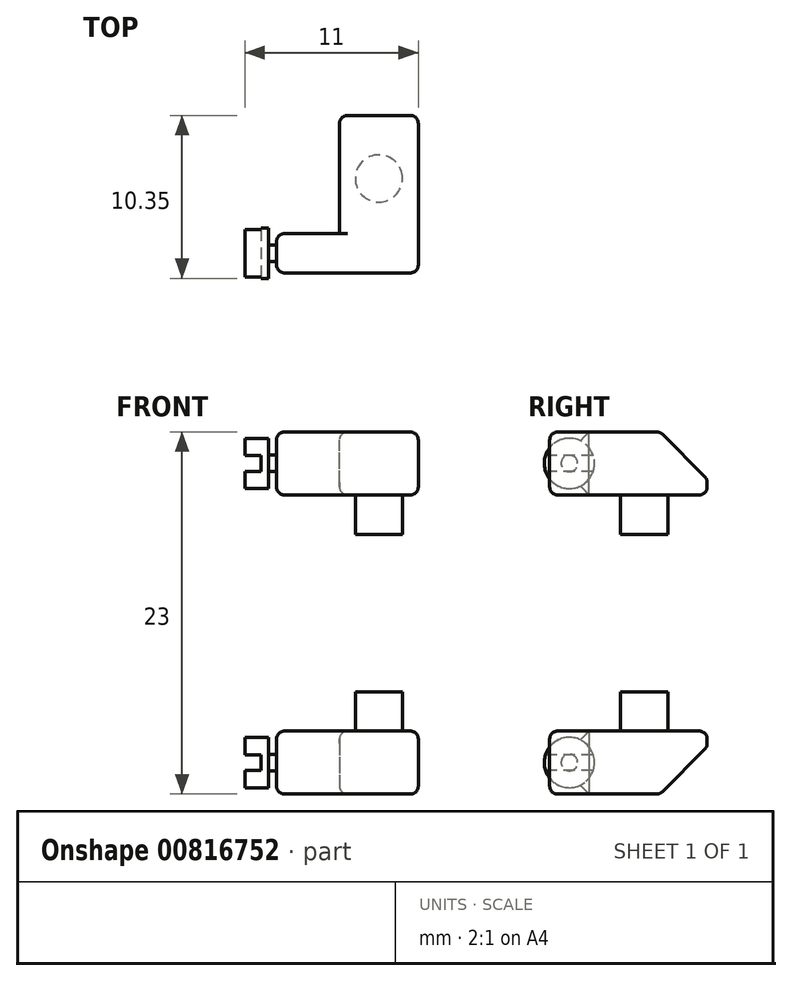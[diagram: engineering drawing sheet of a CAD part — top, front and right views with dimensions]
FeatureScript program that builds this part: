
annotation { "Feature Type Name" : "Feature", "Feature Type Description" : "" }
export const myFeature = defineFeature(function(context is Context, id is Id, definition is map)
    precondition{}
    {
        {
            var Q0;
            Q0=qCreatedBy(makeId("Top.planeOp"),FACE);
            var sketch = newSketch(context, id + "F0", { "sketchPlane" : qUnion([Q0])});
            skLineSegment(sketch, "E0.bottom", {"start": v(-2.5, 5) * mm, "end": v(2.5, 5) * mm});
            skLineSegment(sketch, "E0.top", {"start": v(-2.5, -5) * mm, "end": v(2.5, -5) * mm});
            skLineSegment(sketch, "E0.left", {"start": v(-2.5, 5) * mm, "end": v(-2.5, -5) * mm});
            skLineSegment(sketch, "E0.right", {"start": v(2.5, 5) * mm, "end": v(2.5, -5) * mm});
            skPoint(sketch, "E0.middle", {"position": v(0, 0) * mm});
            skSolve(sketch);
        }
        {
            var Q0;
            Q0 = qSketchRegion(id + "F0", true);
            extrude(context, id + "F1", {"entities" : qUnion([Q0]), "depth" : 4 * mm, "offsetDistance" : 25 * mm});
        }
        {
            var Q0;
            Q0=makeQuery(id+"F1.opExtrude","CAP_EDGE",EDGE,{"disambiguationData":[OSD([sQuery(id+"F0.wireOp",EDGE,"E0.bottom")])],"isStart":false});
            chamfer(context, id + "F2", {"entities" : qUnion([Q0]), "width" : 3 * mm, "tangentPropagation" : true});
        }
        {
            var Q0;
            Q0=makeQuery(id+"F1.opExtrude","CAP_FACE",FACE,{"disambiguationData":[OSD([sQuery(id+"F0.wireOp",EDGE,"E0.bottom"),sQuery(id+"F0.wireOp",EDGE,"E0.top"),sQuery(id+"F0.wireOp",EDGE,"E0.left"),sQuery(id+"F0.wireOp",EDGE,"E0.right")])],"isStart":true});
            var sketch = newSketch(context, id + "F3", { "sketchPlane" : qUnion([Q0])});
            skCircle(sketch, "E1", {"center": v(0, -1) * mm, "radius": 1.5 * mm});
            skPoint(sketch, "E2.start.orphan", {"position": v(0, 0) * mm});
            skSolve(sketch);
        }
        {
            var Q0;
            Q0 = qSketchRegion(id + "F3", true);
            extrude(context, id + "F4", {"entities" : qUnion([Q0]), "operationType" : NewBodyOperationType.ADD, "depth" : 2.5 * mm, "offsetDistance" : 25 * mm});
        }
        {
            var Q0;
            Q0=makeQuery(id+"F1.opExtrude","SWEPT_FACE",FACE,{"disambiguationData":[OSD([sQuery(id+"F0.wireOp",EDGE,"E0.left")])]});
            var sketch = newSketch(context, id + "F5", { "sketchPlane" : qUnion([Q0])});
            skLineSegment(sketch, "E3.bottom", {"start": v(5, 0) * mm, "end": v(2.5, 0) * mm});
            skLineSegment(sketch, "E3.top", {"start": v(5, 4) * mm, "end": v(2.5, 4) * mm});
            skLineSegment(sketch, "E3.left", {"start": v(5, 0) * mm, "end": v(5, 4) * mm});
            skLineSegment(sketch, "E3.right", {"start": v(2.5, 0) * mm, "end": v(2.5, 4) * mm});
            skSolve(sketch);
        }
        {
            var Q0;
            {var subQ0=sQuery(id+"F5.wireOp",EDGE,"E3.bottom");Q0=makeQuery(id+"F5.imprint","IMPRINT",FACE,{"disambiguationData":[TD([[makeQuery(id+"F5.imprint","IMPRINT",EDGE,{"derivedFrom":subQ0}),-1.0]])]});}
            var Q1;
            {var subQ0=sQuery(id+"F5.wireOp",EDGE,"E3.left");var subQ1=sQuery(id+"F0.wireOp",EDGE,"E0.left");var subQ2=makeQuery(id+"F1.opExtrude","SWEPT_FACE",FACE,{"disambiguationData":[OSD([subQ1])]});var subQ3=makeQuery(id+"FWwU1mPq5ux4r18_1.opFillet","BLEND_EDGE",EDGE,{"blendedFrom":[makeQuery(id+"F1.opExtrude","CAP_EDGE",EDGE,{"disambiguationData":[OSD([subQ1])],"isStart":true}),subQ2],"blendedInto":[subQ2]});var subQ4=makeQuery(id+"F5.imprint","INTERSECT",VERTEX,{"derivedFrom":[subQ3,subQ0]});var subQ5=makeQuery(id+"FWwU1mPq5ux4r18_1.opFillet","BLEND_EDGE",EDGE,{"blendedFrom":[makeQuery(id+"F1.opExtrude","CAP_EDGE",EDGE,{"disambiguationData":[OSD([subQ1])],"isStart":false}),subQ2],"blendedInto":[subQ2]});var subQ6=makeQuery(id+"F5.imprint","INTERSECT",VERTEX,{"derivedFrom":[subQ5,subQ0]});Q1=makeQuery(id+"F5.imprint","IMPRINT",FACE,{"disambiguationData":[TD([[makeQuery(id+"F5.imprint","IMPRINT",EDGE,{"disambiguationData":[TD([[subQ4,1.0],[subQ6,-1.0]])],"derivedFrom":subQ0}),-1.0]])]});}
            var Q2;
            {var subQ0=sQuery(id+"F5.wireOp",EDGE,"E3.top");Q2=makeQuery(id+"F5.imprint","IMPRINT",FACE,{"disambiguationData":[TD([[makeQuery(id+"F5.imprint","IMPRINT",EDGE,{"derivedFrom":subQ0}),1.0]])]});}
            extrude(context, id + "F6", {"entities" : qUnion([Q0, Q1, Q2]), "operationType" : NewBodyOperationType.ADD, "depth" : 4 * mm, "offsetDistance" : 25 * mm});
        }
        {
            var Q0;
            Q0=makeQuery(id+"F6.opExtrude","CAP_EDGE",EDGE,{"disambiguationData":[OSD([sQuery(id+"F5.wireOp",EDGE,"E3.right")])],"isStart":true});
            var Q1;
            Q1=makeQuery(id+"F1.opExtrude","SWEPT_EDGE",EDGE,{"disambiguationData":[OSD([sQuery(id+"F0.wireOp",EDGE,"E0.top"),sQuery(id+"F0.wireOp",EDGE,"E0.right")])]});
            var Q2;
            Q2=makeQuery(id+"F1.opExtrude","CAP_EDGE",EDGE,{"disambiguationData":[OSD([sQuery(id+"F0.wireOp",EDGE,"E0.bottom")])],"isStart":true});
            var Q3;
            {var subQ0=sQuery(id+"F0.wireOp",EDGE,"E0.bottom");Q3=makeQuery(id+"F2.opChamfer","BLEND_EDGE",EDGE,{"blendedFrom":[makeQuery(id+"F1.opExtrude","CAP_EDGE",EDGE,{"disambiguationData":[OSD([subQ0])],"isStart":false}),makeQuery(id+"F1.opExtrude","SWEPT_FACE",FACE,{"disambiguationData":[OSD([subQ0])]})],"blendedInto":[makeQuery(id+"F1.opExtrude","SWEPT_FACE",FACE,{"disambiguationData":[OSD([subQ0])]})]});}
            var Q4;
            Q4=makeQuery(id+"F2.opChamfer","BLEND_EDGE",EDGE,{"blendedFrom":[makeQuery(id+"F1.opExtrude","CAP_EDGE",EDGE,{"disambiguationData":[OSD([sQuery(id+"F0.wireOp",EDGE,"E0.bottom")])],"isStart":false}),makeQuery(id+"F1.opExtrude","SWEPT_FACE",FACE,{"disambiguationData":[OSD([sQuery(id+"F0.wireOp",EDGE,"E0.right")])]})],"blendedInto":[makeQuery(id+"F1.opExtrude","SWEPT_FACE",FACE,{"disambiguationData":[OSD([sQuery(id+"F0.wireOp",EDGE,"E0.right")])]})]});
            var Q5;
            {var subQ0=sQuery(id+"F0.wireOp",EDGE,"E0.bottom");Q5=makeQuery(id+"F2.opChamfer","BLEND_EDGE",EDGE,{"blendedFrom":[makeQuery(id+"F1.opExtrude","CAP_EDGE",EDGE,{"disambiguationData":[OSD([subQ0])],"isStart":false}),makeQuery(id+"F1.opExtrude","CAP_FACE",FACE,{"disambiguationData":[OSD([subQ0,sQuery(id+"F0.wireOp",EDGE,"E0.top"),sQuery(id+"F0.wireOp",EDGE,"E0.left"),sQuery(id+"F0.wireOp",EDGE,"E0.right")])],"isStart":false})],"blendedInto":[makeQuery(id+"F1.opExtrude","CAP_FACE",FACE,{"disambiguationData":[OSD([subQ0,sQuery(id+"F0.wireOp",EDGE,"E0.top"),sQuery(id+"F0.wireOp",EDGE,"E0.left"),sQuery(id+"F0.wireOp",EDGE,"E0.right")])],"isStart":false})]});}
            var Q6;
            Q6=makeQuery(id+"F1.opExtrude","SWEPT_EDGE",EDGE,{"disambiguationData":[OSD([sQuery(id+"F0.wireOp",EDGE,"E0.bottom"),sQuery(id+"F0.wireOp",EDGE,"E0.right")])]});
            var Q7;
            Q7=makeQuery(id+"F2.opChamfer","BLEND_EDGE",EDGE,{"blendedFrom":[makeQuery(id+"F1.opExtrude","CAP_EDGE",EDGE,{"disambiguationData":[OSD([sQuery(id+"F0.wireOp",EDGE,"E0.bottom")])],"isStart":false}),makeQuery(id+"F1.opExtrude","SWEPT_FACE",FACE,{"disambiguationData":[OSD([sQuery(id+"F0.wireOp",EDGE,"E0.left")])]})],"blendedInto":[makeQuery(id+"F1.opExtrude","SWEPT_FACE",FACE,{"disambiguationData":[OSD([sQuery(id+"F0.wireOp",EDGE,"E0.left")])]})]});
            var Q8;
            Q8=makeQuery(id+"F1.opExtrude","SWEPT_EDGE",EDGE,{"disambiguationData":[OSD([sQuery(id+"F0.wireOp",EDGE,"E0.bottom"),sQuery(id+"F0.wireOp",EDGE,"E0.left")])]});
            var Q9;
            Q9=makeQuery(id+"F1.opExtrude","CAP_EDGE",EDGE,{"disambiguationData":[OSD([sQuery(id+"F0.wireOp",EDGE,"E0.left")])],"isStart":true});
            var Q10;
            Q10=makeQuery(id+"F1.opExtrude","CAP_EDGE",EDGE,{"disambiguationData":[OSD([sQuery(id+"F0.wireOp",EDGE,"E0.right")])],"isStart":true});
            var Q11;
            Q11=makeQuery(id+"F6.boolean.opBoolean","MERGE",EDGE,{"derivedFrom":[makeQuery(id+"F1.opExtrude","CAP_EDGE",EDGE,{"disambiguationData":[OSD([sQuery(id+"F0.wireOp",EDGE,"E0.top")])],"isStart":true}),makeQuery(id+"F6.opExtrude","SWEPT_EDGE",EDGE,{"disambiguationData":[OSD([sQuery(id+"F5.wireOp",EDGE,"E3.bottom"),sQuery(id+"F5.wireOp",EDGE,"E3.left")])]})]});
            var Q12;
            Q12=makeQuery(id+"F6.boolean.opBoolean","MERGE",EDGE,{"derivedFrom":[makeQuery(id+"F1.opExtrude","CAP_EDGE",EDGE,{"disambiguationData":[OSD([sQuery(id+"F0.wireOp",EDGE,"E0.top")])],"isStart":false}),makeQuery(id+"F6.opExtrude","SWEPT_EDGE",EDGE,{"disambiguationData":[OSD([sQuery(id+"F5.wireOp",EDGE,"E3.top"),sQuery(id+"F5.wireOp",EDGE,"E3.left")])]})]});
            var Q13;
            Q13=makeQuery(id+"F1.opExtrude","CAP_EDGE",EDGE,{"disambiguationData":[OSD([sQuery(id+"F0.wireOp",EDGE,"E0.right")])],"isStart":false});
            var Q14;
            Q14=makeQuery(id+"F1.opExtrude","CAP_EDGE",EDGE,{"disambiguationData":[OSD([sQuery(id+"F0.wireOp",EDGE,"E0.left")])],"isStart":false});
            var Q15;
            Q15=makeQuery(id+"F6.opExtrude","CAP_EDGE",EDGE,{"disambiguationData":[OSD([sQuery(id+"F5.wireOp",EDGE,"E3.left")])],"isStart":false});
            var Q16;
            Q16=makeQuery(id+"F6.opExtrude","CAP_EDGE",EDGE,{"disambiguationData":[OSD([sQuery(id+"F5.wireOp",EDGE,"E3.top")])],"isStart":false});
            var Q17;
            Q17=makeQuery(id+"F6.opExtrude","CAP_EDGE",EDGE,{"disambiguationData":[OSD([sQuery(id+"F5.wireOp",EDGE,"E3.right")])],"isStart":false});
            var Q18;
            Q18=makeQuery(id+"F6.opExtrude","CAP_EDGE",EDGE,{"disambiguationData":[OSD([sQuery(id+"F5.wireOp",EDGE,"E3.bottom")])],"isStart":false});
            fillet(context, id + "F7", {"entities" : qUnion([Q0, Q1, Q2, Q3, Q4, Q5, Q6, Q7, Q8, Q9, Q10, Q11, Q12, Q13, Q14, Q15, Q16, Q17, Q18]), "radius" : 0.5 * mm, "tangentPropagation" : true, "allowEdgeOverflow" : false});
        }
        {
            var Q0;
            Q0=makeQuery(id+"F6.opExtrude","CAP_FACE",FACE,{"disambiguationData":[OSD([sQuery(id+"F5.wireOp",EDGE,"E3.bottom"),sQuery(id+"F5.wireOp",EDGE,"E3.top"),sQuery(id+"F5.wireOp",EDGE,"E3.left"),sQuery(id+"F5.wireOp",EDGE,"E3.right")])],"isStart":false});
            var sketch = newSketch(context, id + "F8", { "sketchPlane" : qUnion([Q0])});
            skCircle(sketch, "E4", {"center": v(3.75, 2) * mm, "radius": 0.53 * mm});
            skPoint(sketch, "E4.centerSnap0", {"position": v(3, 2) * mm});
            skPoint(sketch, "E4.centerSnap1", {"position": v(3.75, 0.5) * mm});
            skSolve(sketch);
        }
        {
            var Q0;
            Q0 = qSketchRegion(id + "F8", true);
            extrude(context, id + "F9", {"entities" : qUnion([Q0]), "operationType" : NewBodyOperationType.ADD, "depth" : 0.5 * mm, "offsetDistance" : 25 * mm});
        }
        {
            var Q0;
            Q0=makeQuery(id+"F9.opExtrude","CAP_FACE",FACE,{"disambiguationData":[OSD([sQuery(id+"F8.wireOp",EDGE,"E4")])],"isStart":false});
            var sketch = newSketch(context, id + "F10", { "sketchPlane" : qUnion([Q0])});
            skCircle(sketch, "E5", {"center": v(3.75, 2) * mm, "radius": 1.6 * mm});
            skSolve(sketch);
        }
        {
            var Q0;
            Q0 = qSketchRegion(id + "F10", true);
            extrude(context, id + "F11", {"entities" : qUnion([Q0]), "operationType" : NewBodyOperationType.ADD, "depth" : 1.5 * mm, "offsetDistance" : 25 * mm});
        }
        {
            var Q0;
            Q0=makeQuery(id+"F11.opExtrude","CAP_FACE",FACE,{"disambiguationData":[OSD([sQuery(id+"F10.wireOp",EDGE,"E5")])],"isStart":false});
            var sketch = newSketch(context, id + "F12", { "sketchPlane" : qUnion([Q0])});
            skLineSegment(sketch, "E6.bottom", {"start": v(1.74, 2.5) * mm, "end": v(5.76, 2.5) * mm});
            skLineSegment(sketch, "E6.top", {"start": v(1.74, 1.5) * mm, "end": v(5.76, 1.5) * mm});
            skLineSegment(sketch, "E6.left", {"start": v(1.74, 2.5) * mm, "end": v(1.74, 1.5) * mm});
            skLineSegment(sketch, "E6.right", {"start": v(5.76, 2.5) * mm, "end": v(5.76, 1.5) * mm});
            skPoint(sketch, "E6.middle", {"position": v(3.75, 2) * mm});
            skSolve(sketch);
        }
        {
            var Q0;
            Q0 = qSketchRegion(id + "F12", true);
            extrude(context, id + "F13", {"entities" : qUnion([Q0]), "operationType" : NewBodyOperationType.REMOVE, "oppositeDirection" : true, "depth" : 1 * mm, "offsetDistance" : 25 * mm});
        }
        {
            var Q0;
            Q0=makeQuery(id+"F4.opExtrude","CAP_FACE",FACE,{"disambiguationData":[OSD([sQuery(id+"F3.wireOp",EDGE,"E1")])],"isStart":false});
            cPlane(context, id + "F14", {"entities" : qUnion([Q0]), "cplaneType" : CPlaneType.OFFSET, "offset" : 5 * mm, "width" : 150 * mm, "height" : 150 * mm});
        }
        {
            var Q0;
            Q0=makeQuery(id+"F1.opExtrude","SWEPT_BODY",BODY,{"disambiguationData":[OSD([sQuery(id+"F0.wireOp",EDGE,"E0.bottom"),sQuery(id+"F0.wireOp",EDGE,"E0.top"),sQuery(id+"F0.wireOp",EDGE,"E0.left"),sQuery(id+"F0.wireOp",EDGE,"E0.right")])]});
            var Q1;
            Q1=qCreatedBy(id+"F14.planeOp",FACE);
            mirror(context, id + "F15", {"entities" : qUnion([Q0]), "mirrorPlane" : qUnion([Q1])});
        }
    });
